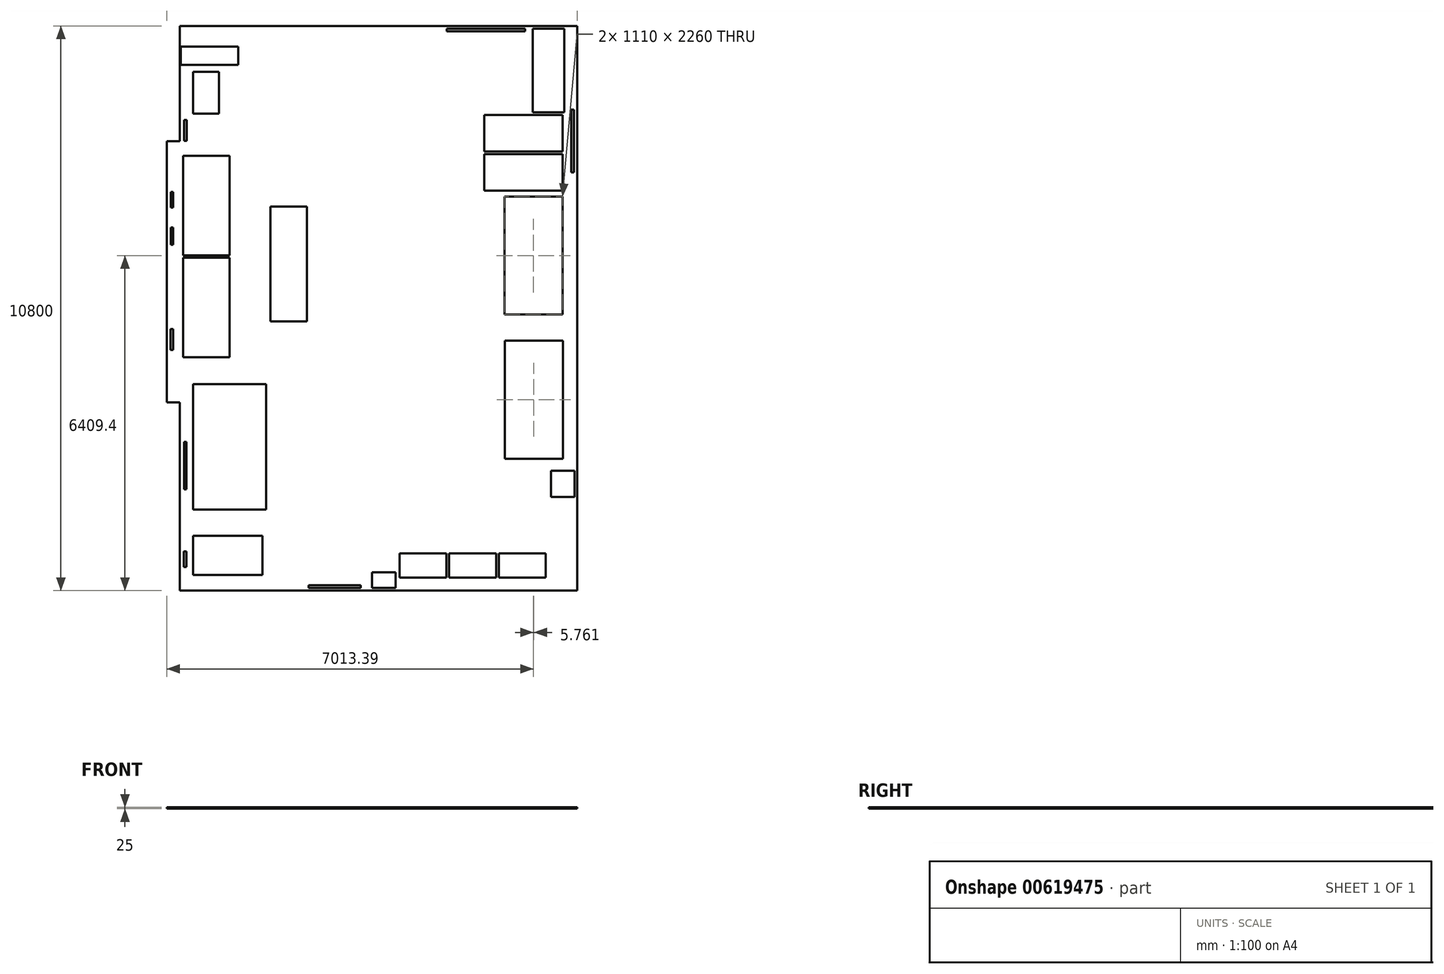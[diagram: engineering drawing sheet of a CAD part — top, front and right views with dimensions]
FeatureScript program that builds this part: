
annotation { "Feature Type Name" : "Feature", "Feature Type Description" : "" }
export const myFeature = defineFeature(function(context is Context, id is Id, definition is map)
    precondition{}
    {
        {
            var Q0;
            Q0=qCreatedBy(makeId("Top.planeOp"),FACE);
            var sketch = newSketch(context, id + "F0", { "sketchPlane" : qUnion([Q0])});
            skLineSegment(sketch, "E0", {"start": v(-5873.53, 5125.43) * mm, "end": v(1326.47, 5125.43) * mm});
            skLineSegment(sketch, "E1", {"start": v(1326.47, 5125.43) * mm, "end": v(1326.47, -5474.57) * mm});
            skLineSegment(sketch, "E2", {"start": v(1326.47, -5474.57) * mm, "end": v(-5873.53, -5474.57) * mm});
            skLineSegment(sketch, "E3", {"start": v(-5873.53, -5474.57) * mm, "end": v(-5873.53, -1874.57) * mm});
            skLineSegment(sketch, "E4", {"start": v(-5873.53, 2725.43) * mm, "end": v(-5873.53, 5125.43) * mm});
            skLineSegment(sketch, "E5", {"start": v(-5873.53, -1874.57) * mm, "end": v(-6123.53, -1874.57) * mm});
            skLineSegment(sketch, "E6", {"start": v(-6123.53, -1874.57) * mm, "end": v(-6123.53, 2725.43) * mm});
            skLineSegment(sketch, "E7", {"start": v(-6123.53, 2725.43) * mm, "end": v(-5873.53, 2725.43) * mm});
            skLineSegment(sketch, "E8", {"start": v(1526.47, -5674.57) * mm, "end": v(-6073.53, -5674.57) * mm});
            skLineSegment(sketch, "E9", {"start": v(-6073.53, -5674.57) * mm, "end": v(-6073.53, -2074.57) * mm});
            skLineSegment(sketch, "E10", {"start": v(-6073.53, -2074.57) * mm, "end": v(-6323.53, -2074.57) * mm});
            skLineSegment(sketch, "E11", {"start": v(-6323.53, -2074.57) * mm, "end": v(-6323.53, 2925.43) * mm});
            skLineSegment(sketch, "E12", {"start": v(-6073.53, 2925.43) * mm, "end": v(-6323.53, 2925.43) * mm});
            skLineSegment(sketch, "E13", {"start": v(-6073.53, 2925.43) * mm, "end": v(-6073.53, 5125.43) * mm});
            skLineSegment(sketch, "E14", {"start": v(-6073.53, 5125.43) * mm, "end": v(-5873.53, 5125.43) * mm});
            skLineSegment(sketch, "E15", {"start": v(1526.47, -5674.57) * mm, "end": v(1526.47, 5125.43) * mm});
            skLineSegment(sketch, "E16", {"start": v(1526.47, 5125.43) * mm, "end": v(1326.47, 5125.43) * mm});
            skLineSegment(sketch, "E17", {"start": v(-973.53, 5075.43) * mm, "end": v(526.47, 5075.43) * mm});
            skLineSegment(sketch, "E18.bottom", {"start": v(-4344.9, 1671.6) * mm, "end": v(-3644.9, 1671.6) * mm});
            skLineSegment(sketch, "E18.top", {"start": v(-4344.9, -528.4) * mm, "end": v(-3644.9, -528.4) * mm});
            skLineSegment(sketch, "E18.left", {"start": v(-4344.9, 1671.6) * mm, "end": v(-4344.9, -528.4) * mm});
            skLineSegment(sketch, "E18.right", {"start": v(-3644.9, 1671.6) * mm, "end": v(-3644.9, -528.4) * mm});
            skLineSegment(sketch, "E19.bottom", {"start": v(-6055.6, 4735.43) * mm, "end": v(-4955.6, 4735.43) * mm});
            skLineSegment(sketch, "E19.top", {"start": v(-6055.6, 4385.43) * mm, "end": v(-4955.6, 4385.43) * mm});
            skLineSegment(sketch, "E19.left", {"start": v(-6055.6, 4735.43) * mm, "end": v(-6055.6, 4385.43) * mm});
            skLineSegment(sketch, "E19.right", {"start": v(-4955.6, 4735.43) * mm, "end": v(-4955.6, 4385.43) * mm});
            skLineSegment(sketch, "E20.bottom", {"start": v(134.86, 1864.84) * mm, "end": v(1244.86, 1864.84) * mm});
            skLineSegment(sketch, "E20.top", {"start": v(134.86, -395.16) * mm, "end": v(1244.86, -395.16) * mm});
            skLineSegment(sketch, "E20.left", {"start": v(134.86, 1864.84) * mm, "end": v(134.86, -395.16) * mm});
            skLineSegment(sketch, "E20.right", {"start": v(1244.86, 1864.84) * mm, "end": v(1244.86, -395.16) * mm});
            skLineSegment(sketch, "E21.bottom", {"start": v(140.62, -895.16) * mm, "end": v(1250.62, -895.16) * mm});
            skLineSegment(sketch, "E21.top", {"start": v(140.62, -3155.16) * mm, "end": v(1250.62, -3155.16) * mm});
            skLineSegment(sketch, "E21.left", {"start": v(140.62, -895.16) * mm, "end": v(140.62, -3155.16) * mm});
            skLineSegment(sketch, "E21.right", {"start": v(1250.62, -895.16) * mm, "end": v(1250.62, -3155.16) * mm});
            skLineSegment(sketch, "E22.bottom", {"start": v(24.83, -4964.57) * mm, "end": v(924.83, -4964.57) * mm});
            skLineSegment(sketch, "E22.top", {"start": v(24.83, -5424.57) * mm, "end": v(924.83, -5424.57) * mm});
            skLineSegment(sketch, "E22.left", {"start": v(24.83, -4964.57) * mm, "end": v(24.83, -5424.57) * mm});
            skLineSegment(sketch, "E22.right", {"start": v(924.83, -4964.57) * mm, "end": v(924.83, -5424.57) * mm});
            skLineSegment(sketch, "E23.bottom", {"start": v(-1875.17, -4964.57) * mm, "end": v(-975.17, -4964.57) * mm});
            skLineSegment(sketch, "E23.top", {"start": v(-1875.17, -5424.57) * mm, "end": v(-975.17, -5424.57) * mm});
            skLineSegment(sketch, "E23.left", {"start": v(-1875.17, -4964.57) * mm, "end": v(-1875.17, -5424.57) * mm});
            skLineSegment(sketch, "E23.right", {"start": v(-975.17, -4964.57) * mm, "end": v(-975.17, -5424.57) * mm});
            skLineSegment(sketch, "E24.bottom", {"start": v(-925.17, -4964.57) * mm, "end": v(-25.17, -4964.57) * mm});
            skLineSegment(sketch, "E24.top", {"start": v(-925.17, -5424.57) * mm, "end": v(-25.17, -5424.57) * mm});
            skLineSegment(sketch, "E24.left", {"start": v(-925.17, -4964.57) * mm, "end": v(-925.17, -5424.57) * mm});
            skLineSegment(sketch, "E24.right", {"start": v(-25.17, -4964.57) * mm, "end": v(-25.17, -5424.57) * mm});
            skLineSegment(sketch, "E25.bottom", {"start": v(-5823.53, -4624.57) * mm, "end": v(-4493.53, -4624.57) * mm});
            skLineSegment(sketch, "E25.top", {"start": v(-5823.53, -5374.57) * mm, "end": v(-4493.53, -5374.57) * mm});
            skLineSegment(sketch, "E25.left", {"start": v(-5823.53, -4624.57) * mm, "end": v(-5823.53, -5374.57) * mm});
            skLineSegment(sketch, "E25.right", {"start": v(-4493.53, -4624.57) * mm, "end": v(-4493.53, -5374.57) * mm});
            skLineSegment(sketch, "E26.bottom", {"start": v(-6012.85, 2640.77) * mm, "end": v(-5122.85, 2640.77) * mm});
            skLineSegment(sketch, "E26.top", {"start": v(-6012.85, 740.77) * mm, "end": v(-5122.85, 740.77) * mm});
            skLineSegment(sketch, "E26.left", {"start": v(-6012.85, 2640.77) * mm, "end": v(-6012.85, 740.77) * mm});
            skLineSegment(sketch, "E26.right", {"start": v(-5122.85, 2640.77) * mm, "end": v(-5122.85, 740.77) * mm});
            skLineSegment(sketch, "E27.bottom", {"start": v(-6012.85, 690.77) * mm, "end": v(-5122.85, 690.77) * mm});
            skLineSegment(sketch, "E27.top", {"start": v(-6012.85, -1209.23) * mm, "end": v(-5122.85, -1209.23) * mm});
            skLineSegment(sketch, "E27.left", {"start": v(-6012.85, 690.77) * mm, "end": v(-6012.85, -1209.23) * mm});
            skLineSegment(sketch, "E27.right", {"start": v(-5122.85, 690.77) * mm, "end": v(-5122.85, -1209.23) * mm});
            skLineSegment(sketch, "E28.bottom", {"start": v(-255.2, 3425.43) * mm, "end": v(1244.8, 3425.43) * mm});
            skLineSegment(sketch, "E28.top", {"start": v(-255.2, 2725.43) * mm, "end": v(1244.8, 2725.43) * mm});
            skLineSegment(sketch, "E28.left", {"start": v(-255.2, 3425.43) * mm, "end": v(-255.2, 2725.43) * mm});
            skLineSegment(sketch, "E28.right", {"start": v(1244.8, 3425.43) * mm, "end": v(1244.8, 2725.43) * mm});
            skLineSegment(sketch, "E29.bottom", {"start": v(-254.23, 2675.43) * mm, "end": v(1245.77, 2675.43) * mm});
            skLineSegment(sketch, "E29.top", {"start": v(-254.23, 1975.43) * mm, "end": v(1245.77, 1975.43) * mm});
            skLineSegment(sketch, "E29.left", {"start": v(-254.23, 2675.43) * mm, "end": v(-254.23, 1975.43) * mm});
            skLineSegment(sketch, "E29.right", {"start": v(1245.77, 2675.43) * mm, "end": v(1245.77, 1975.43) * mm});
            skLineSegment(sketch, "E30.bottom", {"start": v(-2396.3, -5324.57) * mm, "end": v(-1946.3, -5324.57) * mm});
            skLineSegment(sketch, "E30.top", {"start": v(-2396.3, -5624.57) * mm, "end": v(-1946.3, -5624.57) * mm});
            skLineSegment(sketch, "E30.left", {"start": v(-2396.3, -5324.57) * mm, "end": v(-2396.3, -5624.57) * mm});
            skLineSegment(sketch, "E30.right", {"start": v(-1946.3, -5324.57) * mm, "end": v(-1946.3, -5624.57) * mm});
            skLineSegment(sketch, "E31", {"start": v(-973.53, 5075.43) * mm, "end": v(-973.53, 5025.43) * mm});
            skLineSegment(sketch, "E32", {"start": v(-973.53, 5025.43) * mm, "end": v(526.47, 5025.43) * mm});
            skLineSegment(sketch, "E33", {"start": v(526.47, 5025.43) * mm, "end": v(526.47, 5075.43) * mm});
            skLineSegment(sketch, "E34", {"start": v(1409.62, 3525.43) * mm, "end": v(1459.62, 3525.43) * mm});
            skLineSegment(sketch, "E35", {"start": v(1409.62, 3525.43) * mm, "end": v(1409.62, 2325.43) * mm});
            skLineSegment(sketch, "E36", {"start": v(1409.62, 2325.43) * mm, "end": v(1459.62, 2325.43) * mm});
            skLineSegment(sketch, "E37", {"start": v(1459.62, 2325.43) * mm, "end": v(1459.62, 3525.43) * mm});
            skLineSegment(sketch, "E38.bottom", {"start": v(676.47, 5075.43) * mm, "end": v(1276.47, 5075.43) * mm});
            skLineSegment(sketch, "E38.top", {"start": v(676.47, 3475.43) * mm, "end": v(1276.47, 3475.43) * mm});
            skLineSegment(sketch, "E38.left", {"start": v(676.47, 5075.43) * mm, "end": v(676.47, 3475.43) * mm});
            skLineSegment(sketch, "E38.right", {"start": v(1276.47, 5075.43) * mm, "end": v(1276.47, 3475.43) * mm});
            skLineSegment(sketch, "E39.bottom", {"start": v(-5996.22, -2829.57) * mm, "end": v(-5946.22, -2829.57) * mm});
            skLineSegment(sketch, "E39.top", {"start": v(-5996.22, -3739.57) * mm, "end": v(-5946.22, -3739.57) * mm});
            skLineSegment(sketch, "E39.left", {"start": v(-5996.22, -2829.57) * mm, "end": v(-5996.22, -3739.57) * mm});
            skLineSegment(sketch, "E39.right", {"start": v(-5946.22, -2829.57) * mm, "end": v(-5946.22, -3739.57) * mm});
            skLineSegment(sketch, "E40.bottom", {"start": v(-6251.2, -674.57) * mm, "end": v(-6201.2, -674.57) * mm});
            skLineSegment(sketch, "E40.top", {"start": v(-6251.2, -1074.57) * mm, "end": v(-6201.2, -1074.57) * mm});
            skLineSegment(sketch, "E40.left", {"start": v(-6251.2, -674.57) * mm, "end": v(-6251.2, -1074.57) * mm});
            skLineSegment(sketch, "E40.right", {"start": v(-6201.2, -674.57) * mm, "end": v(-6201.2, -1074.57) * mm});
            skLineSegment(sketch, "E41.bottom", {"start": v(-6001.47, -4924.57) * mm, "end": v(-5951.47, -4924.57) * mm});
            skLineSegment(sketch, "E41.top", {"start": v(-6001.47, -5224.57) * mm, "end": v(-5951.47, -5224.57) * mm});
            skLineSegment(sketch, "E41.left", {"start": v(-6001.47, -4924.57) * mm, "end": v(-6001.47, -5224.57) * mm});
            skLineSegment(sketch, "E41.right", {"start": v(-5951.47, -4924.57) * mm, "end": v(-5951.47, -5224.57) * mm});
            skLineSegment(sketch, "E42.bottom", {"start": v(-6249.55, 1270.43) * mm, "end": v(-6199.55, 1270.43) * mm});
            skLineSegment(sketch, "E42.top", {"start": v(-6249.55, 940.43) * mm, "end": v(-6199.55, 940.43) * mm});
            skLineSegment(sketch, "E42.left", {"start": v(-6249.55, 1270.43) * mm, "end": v(-6249.55, 940.43) * mm});
            skLineSegment(sketch, "E42.right", {"start": v(-6199.55, 1270.43) * mm, "end": v(-6199.55, 940.43) * mm});
            skLineSegment(sketch, "E43.bottom", {"start": v(-6250.38, 1952.43) * mm, "end": v(-6200.38, 1952.43) * mm});
            skLineSegment(sketch, "E43.top", {"start": v(-6250.38, 1652.43) * mm, "end": v(-6200.38, 1652.43) * mm});
            skLineSegment(sketch, "E43.left", {"start": v(-6250.38, 1952.43) * mm, "end": v(-6250.38, 1652.43) * mm});
            skLineSegment(sketch, "E43.right", {"start": v(-6200.38, 1952.43) * mm, "end": v(-6200.38, 1652.43) * mm});
            skLineSegment(sketch, "E44.bottom", {"start": v(-5990.77, 3328.21) * mm, "end": v(-5940.77, 3328.21) * mm});
            skLineSegment(sketch, "E44.top", {"start": v(-5990.77, 2928.21) * mm, "end": v(-5940.77, 2928.21) * mm});
            skLineSegment(sketch, "E44.left", {"start": v(-5990.77, 3328.21) * mm, "end": v(-5990.77, 2928.21) * mm});
            skLineSegment(sketch, "E44.right", {"start": v(-5940.77, 3328.21) * mm, "end": v(-5940.77, 2928.21) * mm});
            skLineSegment(sketch, "E45.bottom", {"start": v(-5823.53, 4249.26) * mm, "end": v(-5323.53, 4249.26) * mm});
            skLineSegment(sketch, "E45.top", {"start": v(-5823.53, 3449.26) * mm, "end": v(-5323.53, 3449.26) * mm});
            skLineSegment(sketch, "E45.left", {"start": v(-5823.53, 4249.26) * mm, "end": v(-5823.53, 3449.26) * mm});
            skLineSegment(sketch, "E45.right", {"start": v(-5323.53, 4249.26) * mm, "end": v(-5323.53, 3449.26) * mm});
            skLineSegment(sketch, "E46.bottom", {"start": v(1026.47, -3384.57) * mm, "end": v(1476.47, -3384.57) * mm});
            skLineSegment(sketch, "E46.top", {"start": v(1026.47, -3884.57) * mm, "end": v(1476.47, -3884.57) * mm});
            skLineSegment(sketch, "E46.left", {"start": v(1026.47, -3384.57) * mm, "end": v(1026.47, -3884.57) * mm});
            skLineSegment(sketch, "E46.right", {"start": v(1476.47, -3384.57) * mm, "end": v(1476.47, -3884.57) * mm});
            skLineSegment(sketch, "E47.bottom", {"start": v(-5823.53, -1724.57) * mm, "end": v(-4423.53, -1724.57) * mm});
            skLineSegment(sketch, "E47.top", {"start": v(-5823.53, -4124.57) * mm, "end": v(-4423.53, -4124.57) * mm});
            skLineSegment(sketch, "E47.left", {"start": v(-5823.53, -1724.57) * mm, "end": v(-5823.53, -4124.57) * mm});
            skLineSegment(sketch, "E47.right", {"start": v(-4423.53, -1724.57) * mm, "end": v(-4423.53, -4124.57) * mm});
            skLineSegment(sketch, "E48.bottom", {"start": v(-3612.69, -5574.57) * mm, "end": v(-2612.69, -5574.57) * mm});
            skLineSegment(sketch, "E48.top", {"start": v(-3612.69, -5624.57) * mm, "end": v(-2612.69, -5624.57) * mm});
            skLineSegment(sketch, "E48.left", {"start": v(-3612.69, -5574.57) * mm, "end": v(-3612.69, -5624.57) * mm});
            skLineSegment(sketch, "E48.right", {"start": v(-2612.69, -5574.57) * mm, "end": v(-2612.69, -5624.57) * mm});
            skSolve(sketch);
        }
        {
            var Q0;
            Q0 = qSketchRegion(id + "F0", true);
            extrude(context, id + "F1", {"entities" : qUnion([Q0]), "depth" : 25 * mm, "offsetDistance" : 25 * mm});
        }
    });
